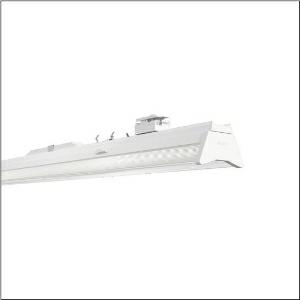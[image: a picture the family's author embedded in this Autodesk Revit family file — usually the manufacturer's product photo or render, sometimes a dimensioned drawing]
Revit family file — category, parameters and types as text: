
# Revit family: licross_11_performance_ho_51td16mn4gxm
name_source: partatom
category: Lighting Fixtures
units: mm (PartAtom-declared; Revit-internal decimal feet)

## family parameters
Cut with Voids When Loaded = No
Host = Face
Light Source = No
Part Type = Normal
Room Calculation Point = No
Round Connector Dimension = Use Diameter
Shared = No

## types (1)
- --- (1 x LED, 16020 lm, 87.4 W, 4000K)
    Apparent Load = 87 VA
    CIE Flux Codes = 63 87 95 78 100
    Color Rendering = 80
    Color Temperature = 4000K
    Default Elevation = 1800 mm
    Description = Licross 11 Performance HO, luminaire insert, of sheet steel, galvanised, coil coated, white, length: 1.500mm, width: 120mm, height: 123mm, LED rated luminous flux: 16.020lm, light colour: 840, SDCM (Standard Deviation of Colour Matching)MacAdam ≤ 2 SDCM (initial), control gear: ON/OFF Multilumen, with plug, 3-pole, with phase selection, mains connection: 220..240V, AC, 50/60Hz, rated input power: 87W, internal wiring halogen-free, primary light control with lens, of plastic, primary optical cover: cover, of PMMA, light emission: direct/indirect distribution, primary light characteristic: symmetric, protection rating (complete): IP54, insulation class (complete): insulation class I (protective earthing), certification: CE, ENEC, VDE, UKCA, protection symbol: D if used in an environment with non-conductive dust loads with corresponding accessories, impact resistance: IK06, permissible ambient temperature for indoor applications: -35..+35°C, corresponds to IFS (International Featured Standards) requirements for safety and quality in the food industry, reducing of maximum allowable ambient temperature of 5°C with ceiling mounting, LABS conformity tested according to VDMA 24364:2018-05, The light source and the operating device comply with the requirements of the Ecodesign Regulation (EU) 2019/2020 and are replaceable in accordance with this regulation, packaging unit: 1 piece
    Height = 114 mm
    Lamp = 1 x LED
    Lamp Light Flux = 16020 lm
    Lamp Power = 87.4 W
    Lamp count = 1
    Length = 1500 mm
    Luminous efficacy = 183 lm/W
    Manufacturer = Siteco
    ModVariant = No
    Model = 51TD16MN4GXM
    Mounting Place = Ceiling
    Mounting Type = Pendant
    Number of Poles = 1
    OnlyDefault = Yes
    Power Factor = 1
    Product Name = Licross 11 Performance HO
    Product group = luminaire insert | ceiling pendant
    ProductGroupID = 901
    Protection Class = Protection class I
    Protection Degree = IP 54
    RLX_Detail_Level = 1
    RLX_Emergency_Light_Flux = 0 lm
    RLX_Emergency_Type = 0
    RLX_Emergency_Type_DB = No
    RlxData = <blob elided: 31997 chars, md5=41b26686>
    Socket = socket
    Standby Power = 0 W
    System Light Flux = 16020 lm
    System Power = 87 W
    Type Comments = factory setting: luminous flux: 100 % | (A | C | E) | 203 mA
    Type Image = l_1256138.jpg
    URL = http://relux.com
    VarID = @adj_090591
    Voltage = 0 V
    Weight = 0.00 kg
    Width = 120 mm

## geometry (parser evidence)
native form markers: Blend x4, Sweep x12
no freeform markers — native parametric forms only
